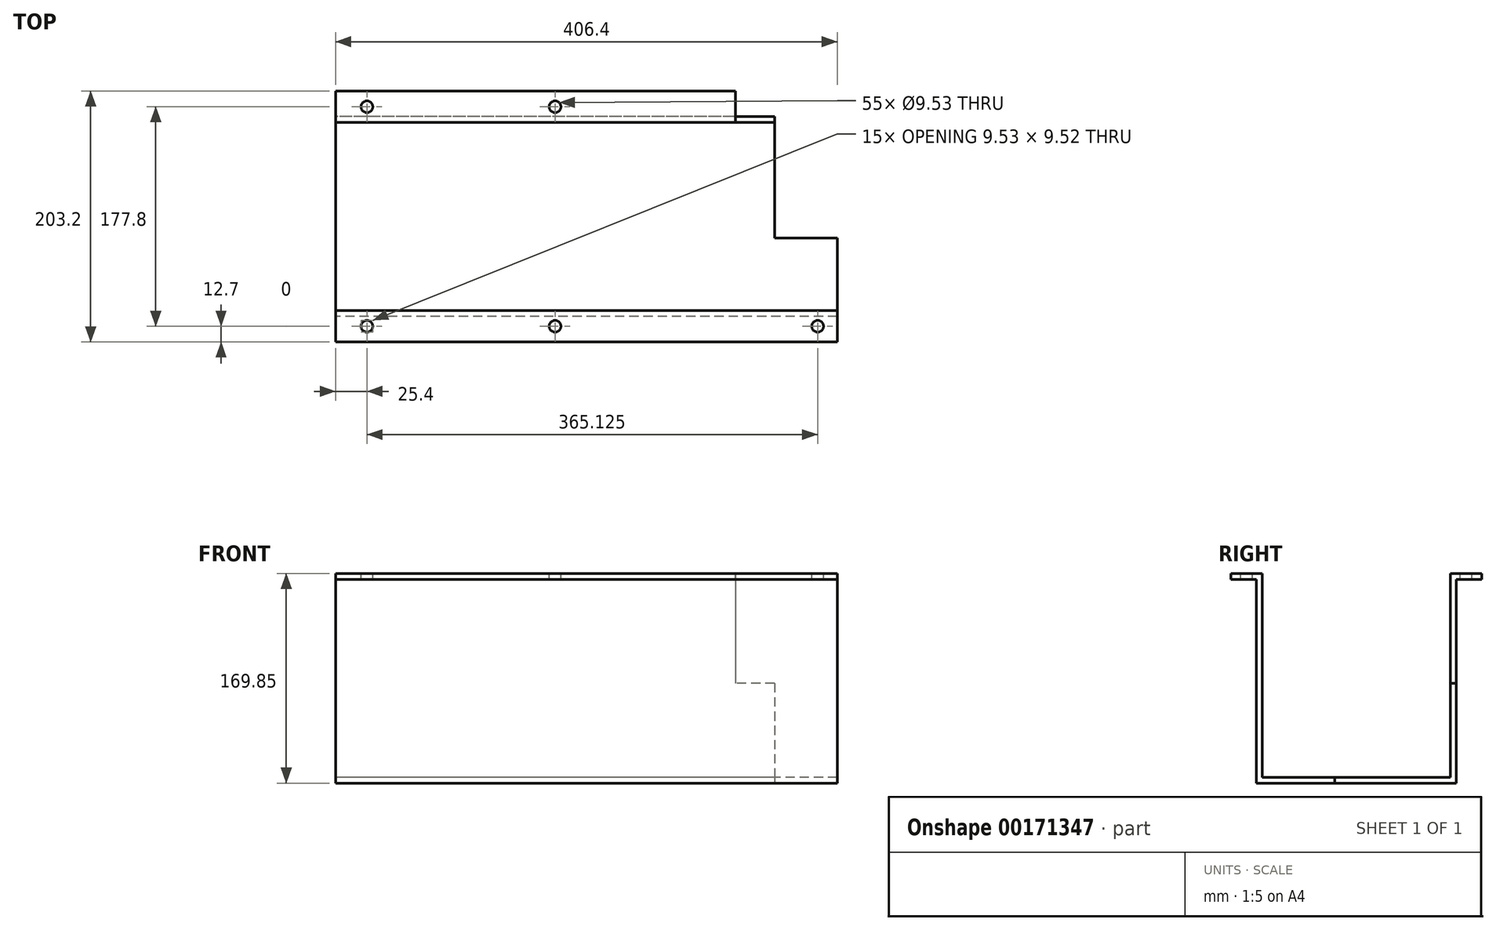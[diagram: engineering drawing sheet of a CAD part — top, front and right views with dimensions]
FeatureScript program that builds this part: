
annotation { "Feature Type Name" : "Feature", "Feature Type Description" : "" }
export const myFeature = defineFeature(function(context is Context, id is Id, definition is map)
    precondition{}
    {
        {
            var Q0;
            Q0=qCreatedBy(makeId("Right.planeOp"),FACE);
            var sketch = newSketch(context, id + "F0", { "sketchPlane" : qUnion([Q0])});
            skLineSegment(sketch, "E0", {"start": v(-76.2, 0) * mm, "end": v(76.2, 0) * mm});
            skPoint(sketch, "E1", {"position": v(0, 0) * mm});
            skLineSegment(sketch, "E2", {"start": v(76.2, 0) * mm, "end": v(76.2, 165.1) * mm});
            skLineSegment(sketch, "E3", {"start": v(76.2, 165.1) * mm, "end": v(101.6, 165.1) * mm});
            skLineSegment(sketch, "E4", {"start": v(-76.2, 0) * mm, "end": v(-76.2, 165.1) * mm});
            skLineSegment(sketch, "E5", {"start": v(-76.2, 165.1) * mm, "end": v(-101.6, 165.1) * mm});
            skLineSegment(sketch, "E6.0", {"start": v(-80.95, 160.35) * mm, "end": v(-101.6, 160.35) * mm});
            skLineSegment(sketch, "E6.1", {"start": v(80.95, 160.35) * mm, "end": v(101.6, 160.35) * mm});
            skLineSegment(sketch, "E6.2", {"start": v(80.95, -4.75) * mm, "end": v(80.95, 160.35) * mm});
            skLineSegment(sketch, "E6.3", {"start": v(-80.95, -4.75) * mm, "end": v(80.95, -4.75) * mm});
            skLineSegment(sketch, "E6.4", {"start": v(-80.95, -4.75) * mm, "end": v(-80.95, 160.35) * mm});
            skLineSegment(sketch, "E7", {"start": v(-101.6, 165.1) * mm, "end": v(-101.6, 160.35) * mm});
            skLineSegment(sketch, "E8", {"start": v(101.6, 165.1) * mm, "end": v(101.6, 160.35) * mm});
            skSolve(sketch);
        }
        {
            var Q0;
            Q0 = qSketchRegion(id + "F0", true);
            extrude(context, id + "F1", {"entities" : qUnion([Q0]), "endBound" : BoundingType.SYMMETRIC, "depth" : 406.4 * mm});
        }
        {
            var Q0;
            Q0=qCreatedBy(makeId("Front.planeOp"),FACE);
            var sketch = newSketch(context, id + "F2", { "sketchPlane" : qUnion([Q0])});
            skLineSegment(sketch, "E9.bottom", {"start": v(203.2, 165.1) * mm, "end": v(120.65, 165.1) * mm});
            skLineSegment(sketch, "E9.top", {"start": v(203.2, 76.2) * mm, "end": v(120.65, 76.2) * mm});
            skLineSegment(sketch, "E9.left", {"start": v(203.2, 165.1) * mm, "end": v(203.2, 76.2) * mm});
            skLineSegment(sketch, "E9.right", {"start": v(120.65, 165.1) * mm, "end": v(120.65, 76.2) * mm});
            skSolve(sketch);
        }
        {
            var Q0;
            Q0 = qSketchRegion(id + "F2", true);
            extrude(context, id + "F3", {"entities" : qUnion([Q0]), "operationType" : NewBodyOperationType.REMOVE, "endBound" : BoundingType.THROUGH_ALL, "oppositeDirection" : true, "depth" : 25.4 * mm});
        }
        {
            var Q0;
            Q0=makeQuery(id+"F1.opExtrude","SWEPT_FACE",FACE,{"disambiguationData":[OSD([sQuery(id+"F0.wireOp",EDGE,"E6.3")])]});
            var sketch = newSketch(context, id + "F4", { "sketchPlane" : qUnion([Q0])});
            skLineSegment(sketch, "E10.bottom", {"start": v(152.4, 17.45) * mm, "end": v(203.2, 17.45) * mm});
            skLineSegment(sketch, "E10.top", {"start": v(152.4, -80.95) * mm, "end": v(203.2, -80.95) * mm});
            skLineSegment(sketch, "E10.left", {"start": v(152.4, 17.45) * mm, "end": v(152.4, -80.95) * mm});
            skLineSegment(sketch, "E10.right", {"start": v(203.2, 17.45) * mm, "end": v(203.2, -80.95) * mm});
            skSolve(sketch);
        }
        {
            var Q0;
            Q0 = qSketchRegion(id + "F4", true);
            extrude(context, id + "F5", {"entities" : qUnion([Q0]), "operationType" : NewBodyOperationType.REMOVE, "endBound" : BoundingType.THROUGH_ALL, "oppositeDirection" : true, "depth" : 25.4 * mm});
        }
        {
            var Q0;
            Q0=makeQuery(id+"F1.opExtrude","SWEPT_FACE",FACE,{"disambiguationData":[OSD([sQuery(id+"F0.wireOp",EDGE,"E3")])]});
            var sketch = newSketch(context, id + "F6", { "sketchPlane" : qUnion([Q0])});
            skLineSegment(sketch, "E11.bottom", {"start": v(-177.8, 88.9) * mm, "end": v(-25.4, 88.9) * mm, "construction": true});
            skLineSegment(sketch, "E11.top", {"start": v(-177.8, -88.9) * mm, "end": v(-25.4, -88.9) * mm, "construction": true});
            skLineSegment(sketch, "E11.left", {"start": v(-177.8, 88.9) * mm, "end": v(-177.8, -88.9) * mm, "construction": true});
            skLineSegment(sketch, "E11.right", {"start": v(-25.4, 88.9) * mm, "end": v(-25.4, -88.9) * mm, "construction": true});
            skCircle(sketch, "E12", {"center": v(-177.8, 88.9) * mm, "radius": 4.76 * mm});
            skCircle(sketch, "E13", {"center": v(-25.4, 88.9) * mm, "radius": 4.76 * mm});
            skCircle(sketch, "E14", {"center": v(-177.8, -88.9) * mm, "radius": 4.76 * mm});
            skCircle(sketch, "E15", {"center": v(-25.4, -88.9) * mm, "radius": 4.76 * mm});
            skCircle(sketch, "E16", {"center": v(187.33, -88.9) * mm, "radius": 4.76 * mm});
            skSolve(sketch);
        }
        {
            var Q0;
            Q0 = qSketchRegion(id + "F6", true);
            extrude(context, id + "F7", {"entities" : qUnion([Q0]), "operationType" : NewBodyOperationType.REMOVE, "endBound" : BoundingType.THROUGH_ALL, "oppositeDirection" : true, "depth" : 25.4 * mm});
        }
    });
